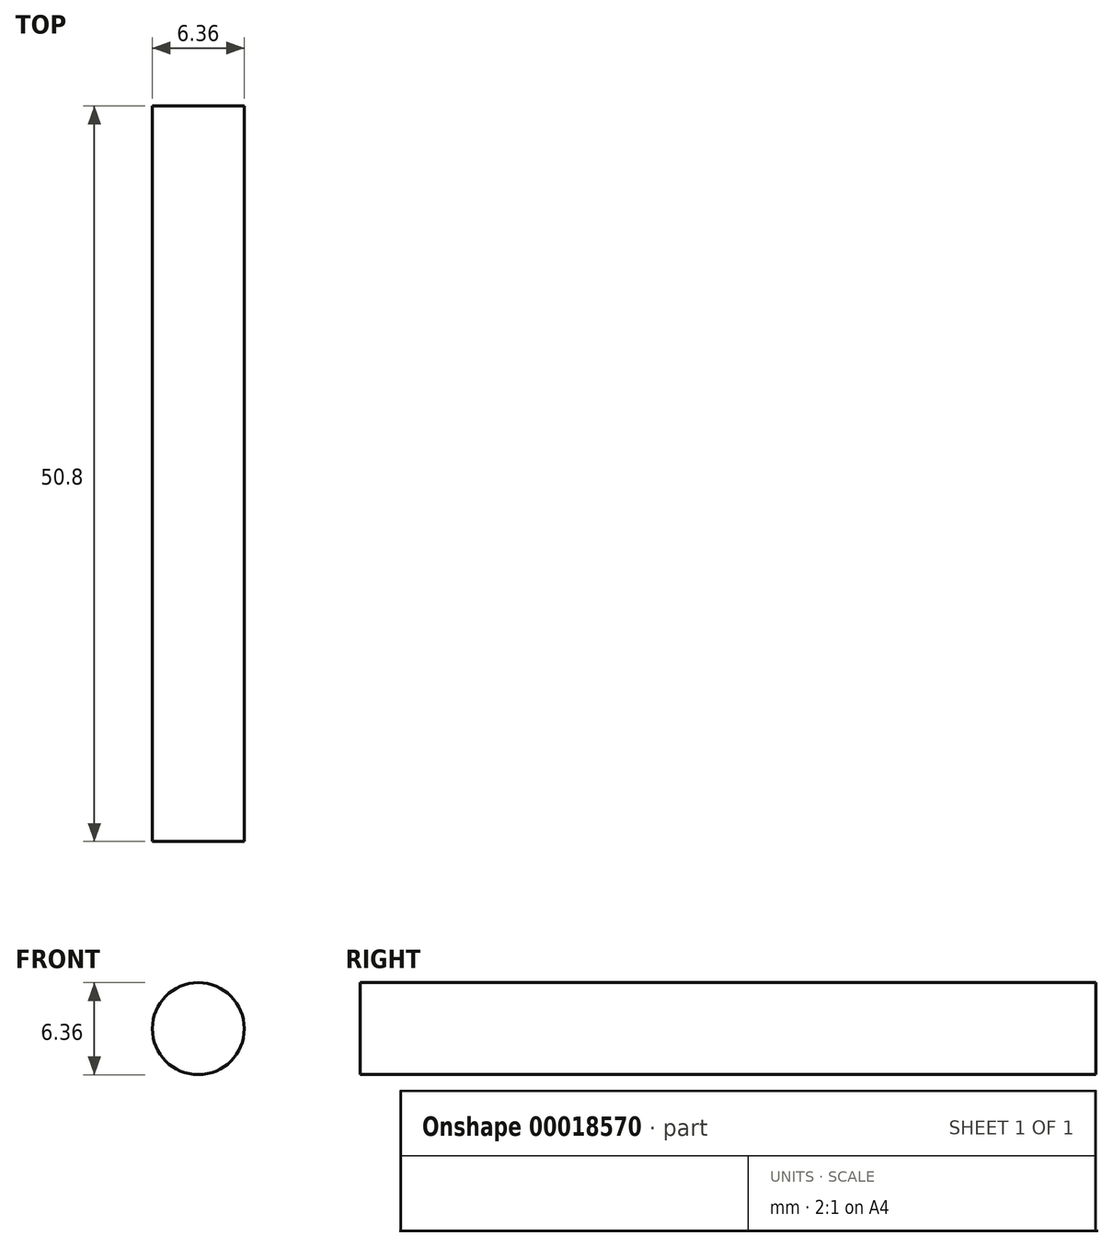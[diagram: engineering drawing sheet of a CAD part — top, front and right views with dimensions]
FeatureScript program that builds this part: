
annotation { "Feature Type Name" : "Feature", "Feature Type Description" : "" }
export const myFeature = defineFeature(function(context is Context, id is Id, definition is map)
    precondition{}
    {
        {
            var Q0;
            Q0=qCreatedBy(makeId("Front.planeOp"),FACE);
            var sketch = newSketch(context, id + "F1", { "sketchPlane" : qUnion([Q0])});
            skCircle(sketch, "E0", {"center": v(0, 0) * mm, "radius": 3.18 * mm});
            skSolve(sketch);
        }
        {
            var Q0;
            Q0 = qSketchRegion(id + "F1", true);
            extrude(context, id + "F0", {"entities" : qUnion([Q0]), "depth" : 50.8 * mm});
        }
    });
